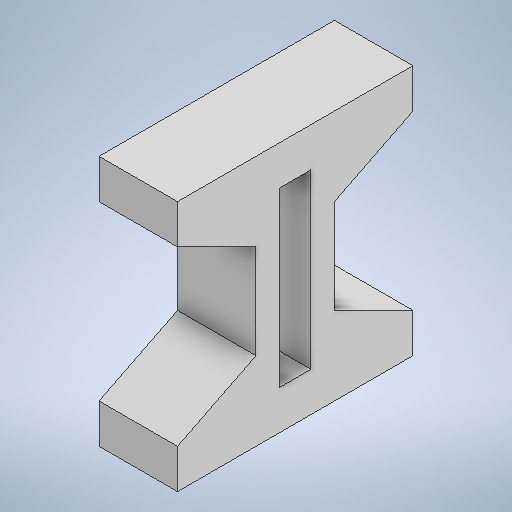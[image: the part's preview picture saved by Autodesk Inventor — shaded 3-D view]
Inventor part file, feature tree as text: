
AUTODESK INVENTOR PART (.ipt)
format: ipt  version: 2025.2 (Build 292293000, 293)  size: 262,144 bytes
history: native  units: in
note: dims shown in document units (in); Inventor stores cm internally (conversion verified against a paired STEP export)
features: extrude x4, sketch x4
ambient origin geometry x8: Origin, YZ Plane, XZ Plane, XY Plane, X Axis, Y Axis, Z Axis, Center Point
bodies: Solid1 (feature_tree)
feature tree (8):
  extrude  "Extrusion1"  Depth=0.3937in
  extrude  "Extrusion2"  Depth=0.3937in
  extrude  "Extrusion3"  Depth=0.3937in
  extrude  "Extrusion4"  Depth=0.3937in
  sketch  "Sketch1"  dims[d0=0.3937in d1=0.3937in]
  sketch  "Sketch2"  dims[d2=1.2598in d3=0.0in d4=0.3937in]
  sketch  "Sketch3"  dims[d5=0.3937in d6=0.3937in]
  sketch  "Sketch4"  dims[d7=0.3937in d8=0.0in d9=0.3937in d10=0.3937in d11=0.3937in d12=0.3937in d13=0.0in d14=0.1969in d15=0.1969in d16=0.1181in d17=0.1181in d18=0.3937in d19=0.0in]
